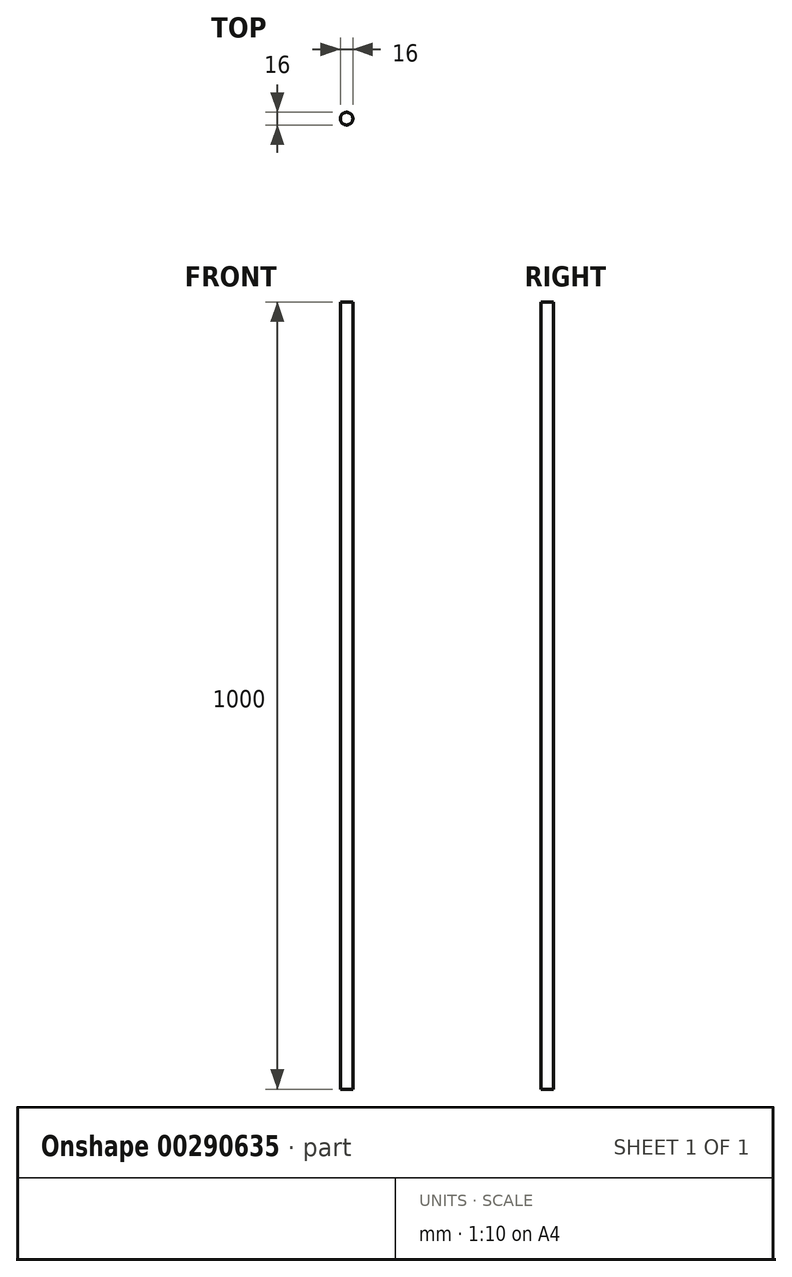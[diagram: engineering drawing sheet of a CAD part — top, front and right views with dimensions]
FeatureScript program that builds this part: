
annotation { "Feature Type Name" : "Feature", "Feature Type Description" : "" }
export const myFeature = defineFeature(function(context is Context, id is Id, definition is map)
    precondition{}
    {
        {
            var Q0;
            Q0=qCreatedBy(makeId("Top.planeOp"),FACE);
            var sketch = newSketch(context, id + "F0", { "sketchPlane" : qUnion([Q0])});
            skCircle(sketch, "E0", {"center": v(0, 0) * mm, "radius": 8 * mm});
            skSolve(sketch);
        }
        {
            var Q0;
            Q0 = qSketchRegion(id + "F0", true);
            extrude(context, id + "F1", {"entities" : qUnion([Q0]), "depth" : 1000 * mm});
        }
    });
